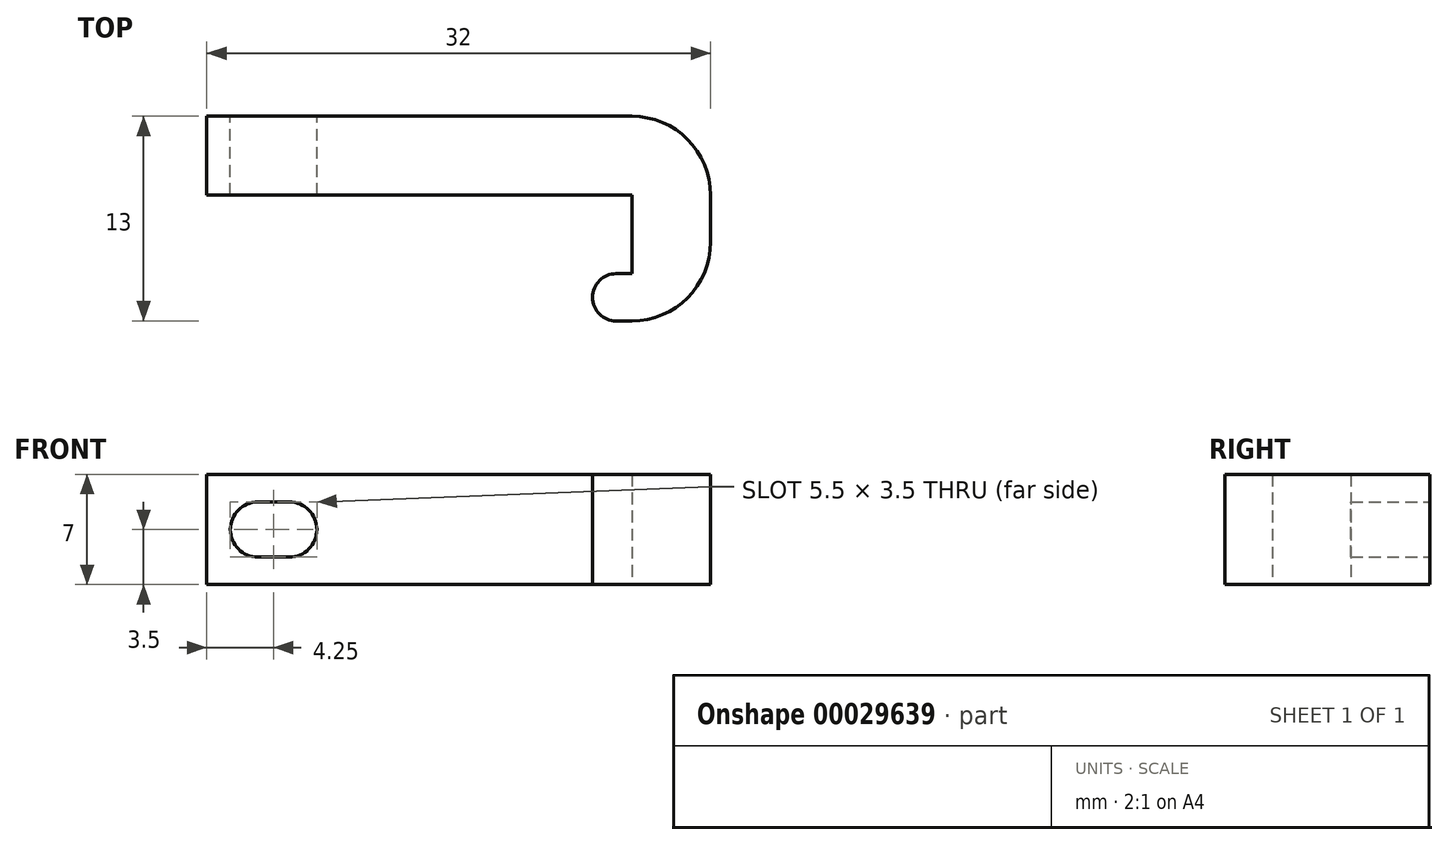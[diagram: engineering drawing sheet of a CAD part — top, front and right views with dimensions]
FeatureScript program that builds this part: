
annotation { "Feature Type Name" : "Feature", "Feature Type Description" : "" }
export const myFeature = defineFeature(function(context is Context, id is Id, definition is map)
    precondition{}
    {
        {
            var Q0;
            Q0=qCreatedBy(makeId("Top.planeOp"),FACE);
            var sketch = newSketch(context, id + "F0", { "sketchPlane" : qUnion([Q0])});
            skLineSegment(sketch, "E0", {"start": v(0, 0) * mm, "end": v(5, 0) * mm});
            skLineSegment(sketch, "E1", {"start": v(5, 0) * mm, "end": v(5, 13) * mm});
            skLineSegment(sketch, "E2", {"start": v(5, 13) * mm, "end": v(-27, 13) * mm});
            skLineSegment(sketch, "E3", {"start": v(-27, 13) * mm, "end": v(-27, 8) * mm});
            skLineSegment(sketch, "E4", {"start": v(-27, 8) * mm, "end": v(0, 8) * mm});
            skLineSegment(sketch, "E5", {"start": v(0, 8) * mm, "end": v(0, 3) * mm});
            skLineSegment(sketch, "E6", {"start": v(0, 3) * mm, "end": v(-1, 3) * mm});
            skLineSegment(sketch, "E7", {"start": v(0, 0) * mm, "end": v(-1, 0) * mm});
            skArc(sketch, "E8", {"start": v(-1, 3) * mm, "mid": v(-2.5, 1.5) * mm, "end": v(-1, 0) * mm});
            skSolve(sketch);
        }
        {
            var Q0;
            Q0=qSketchRegion(id+"F0",true);
            extrude(context, id + "F1", {"entities" : qUnion([Q0]), "depth" : 7 * mm});
        }
        {
            var Q0;
            Q0=makeQuery(id+"F1.opExtrude","SWEPT_FACE",FACE,{"disambiguationData":[OSD([sQuery(id+"F0.wireOp",EDGE,"E2")])]});
            var sketch = newSketch(context, id + "F2", { "sketchPlane" : qUnion([Q0])});
            skCircle(sketch, "E9", {"center": v(23.75, 3.5) * mm, "radius": 1.75 * mm});
            skLineSegment(sketch, "E10", {"start": v(23.75, 7) * mm, "end": v(23.75, 0) * mm});
            skCircle(sketch, "E11", {"center": v(21.75, 3.5) * mm, "radius": 1.75 * mm});
            skLineSegment(sketch, "E12", {"start": v(21.75, 5.25) * mm, "end": v(23.75, 5.25) * mm});
            skLineSegment(sketch, "E13", {"start": v(21.75, 1.75) * mm, "end": v(23.75, 1.75) * mm});
            skSolve(sketch);
        }
        {
            var Q0;
            Q0=qSketchRegion(id+"F2",true);
            var Q1;
            {var subQ0=sQuery(id+"F2.wireOp",EDGE,"E11");var subQ1=sQuery(id+"F2.wireOp",EDGE,"E9");var subQ3=makeQuery(id+"F2.imprint","INTERSECT",VERTEX,{"disambiguationData":[OD(0.0)],"derivedFrom":[subQ1,subQ0]});Q1=makeQuery(id+"F2.imprint","IMPRINT",FACE,{"disambiguationData":[TD([[makeQuery(id+"F2.imprint","IMPRINT",EDGE,{"disambiguationData":[TD([[subQ3,-1.0]])],"derivedFrom":subQ1}),1.0]])]});}
            extrude(context, id + "F3", {"entities" : qUnion([Q0, Q1]), "operationType" : NewBodyOperationType.REMOVE, "oppositeDirection" : true, "depth" : 25 * mm});
        }
        {
            var Q0;
            Q0=makeQuery(id+"F1.opExtrude","SWEPT_EDGE",EDGE,{"disambiguationData":[OSD([sQuery(id+"F0.wireOp",EDGE,"E1"),sQuery(id+"F0.wireOp",EDGE,"E2")])]});
            var Q1;
            Q1=makeQuery(id+"F1.opExtrude","SWEPT_EDGE",EDGE,{"disambiguationData":[OSD([sQuery(id+"F0.wireOp",EDGE,"E0"),sQuery(id+"F0.wireOp",EDGE,"E1")])]});
            fillet(context, id + "F4", {"entities" : qUnion([Q0, Q1]), "radius" : 5 * mm, "tangentPropagation" : true, "allowEdgeOverflow" : false});
        }
    });
